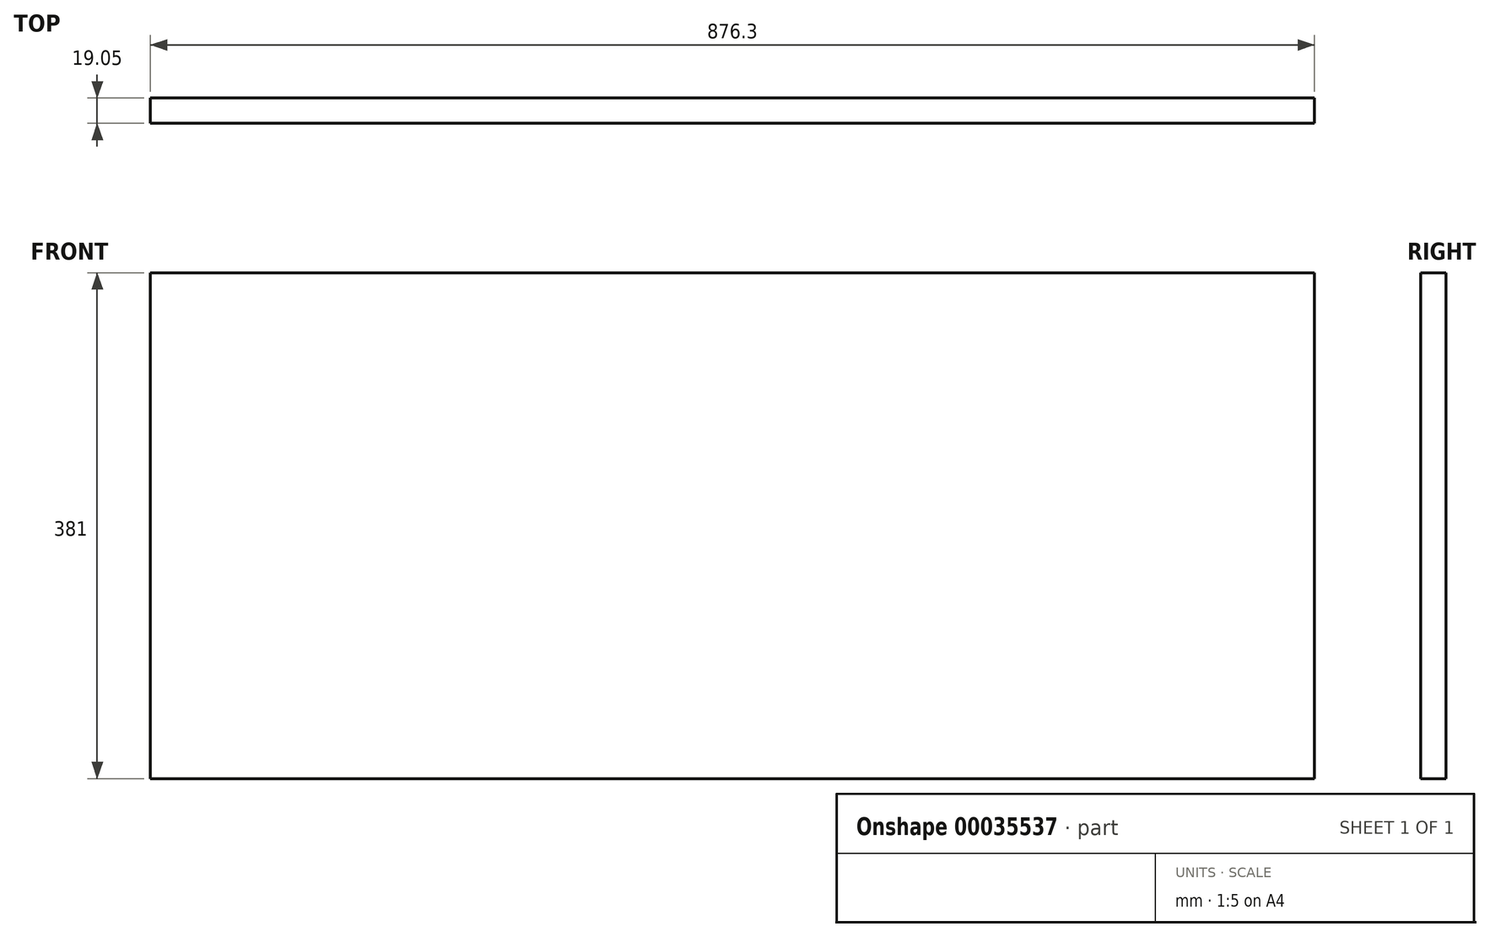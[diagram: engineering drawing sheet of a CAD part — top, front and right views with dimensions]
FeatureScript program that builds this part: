
annotation { "Feature Type Name" : "Feature", "Feature Type Description" : "" }
export const myFeature = defineFeature(function(context is Context, id is Id, definition is map)
    precondition{}
    {
        {
            var Q0;
            Q0=qCreatedBy(makeId("Front.planeOp"),FACE);
            var sketch = newSketch(context, id + "F0", { "sketchPlane" : qUnion([Q0])});
            skLineSegment(sketch, "E0.bottom", {"start": v(-436.47, 112.46) * mm, "end": v(439.83, 112.46) * mm});
            skLineSegment(sketch, "E0.top", {"start": v(-436.47, -268.54) * mm, "end": v(439.83, -268.54) * mm});
            skLineSegment(sketch, "E0.left", {"start": v(-436.47, 112.46) * mm, "end": v(-436.47, -268.54) * mm});
            skLineSegment(sketch, "E0.right", {"start": v(439.83, 112.46) * mm, "end": v(439.83, -268.54) * mm});
            skSolve(sketch);
        }
        {
            var Q0;
            Q0 = qSketchRegion(id + "F0", true);
            extrude(context, id + "F1", {"entities" : qUnion([Q0]), "depth" : 19.05 * mm});
        }
    });
